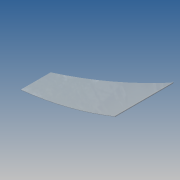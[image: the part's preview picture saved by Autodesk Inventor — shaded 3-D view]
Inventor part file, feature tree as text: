
AUTODESK INVENTOR PART (.ipt)
format: ipt  version: 2014 SP1 (Build 180222100, 222)  size: 169,472 bytes
history: native  units: in
note: dims shown in document units (in); Inventor stores cm internally (conversion verified against a paired STEP export)
features: sketch x4, extrude x2, sweep x1, plane x1, other x1
ambient origin geometry x8: Origin, YZ Plane, XZ Plane, XY Plane, X Axis, Y Axis, Z Axis, Center Point
bodies: Body1 (feature_tree)
feature tree (9):
  sweep  "Sweep2"
  extrude  "Extrusion2"  TaperAngle=0.0deg  [1 undecoded]
  plane  "Work Plane4"
  extrude  "Extrusion3"  Depth=167.1in
  sketch  "Sketch3"  dims[d6=0.0in d7=277.0in d8=60.0in]
  other  "2D Equation Curve2"
  sketch  "Sketch4"  dims[d10=0.25in d11=0.0in]
  sketch  "Sketch7"  dims[d24=78.1in d25=167.1in]
  sketch  "Sketch10"  dims[d26=220.0in d27=1.1853in d28=2.0in d29=2.0in d30=200.0in d31=0.0in d35=167.0in d36=0.25in d37=0.0in]
note: 1 required parameter value undecoded (feature->parameter linkage not recoverable at this tier; creation-order binding heuristic only, values carry confidence <= 0.55)
